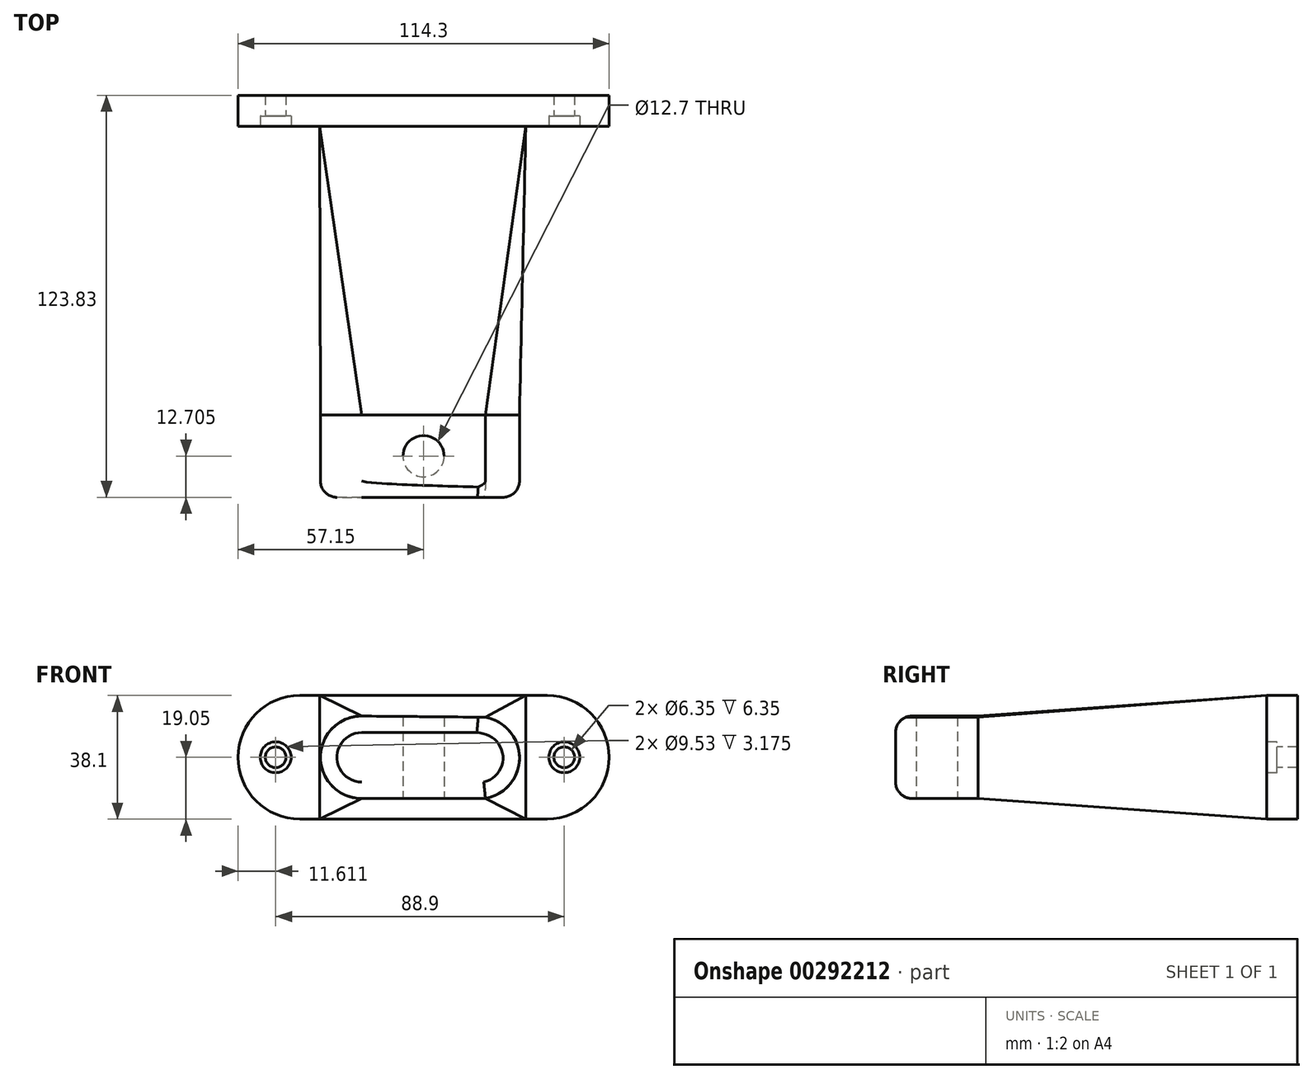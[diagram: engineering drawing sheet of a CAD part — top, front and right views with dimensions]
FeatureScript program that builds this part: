
annotation { "Feature Type Name" : "Feature", "Feature Type Description" : "" }
export const myFeature = defineFeature(function(context is Context, id is Id, definition is map)
    precondition{}
    {
        {
            var Q0;
            Q0=qCreatedBy(makeId("Front.planeOp"),FACE);
            var sketch = newSketch(context, id + "F0", { "sketchPlane" : qUnion([Q0])});
            skArc(sketch, "E0", {"start": v(0, 19.05) * mm, "mid": v(-19.05, 0) * mm, "end": v(0, -19.05) * mm});
            skLineSegment(sketch, "E1", {"start": v(0, 19.05) * mm, "end": v(76.2, 19.05) * mm});
            skArc(sketch, "E2", {"start": v(76.2, -19.05) * mm, "mid": v(95.25, 0) * mm, "end": v(76.2, 19.05) * mm});
            skLineSegment(sketch, "E3", {"start": v(0, -19.05) * mm, "end": v(76.2, -19.05) * mm});
            skSolve(sketch);
        }
        {
            var Q0;
            Q0 = qSketchRegion(id + "F0", true);
            extrude(context, id + "F1", {"entities" : qUnion([Q0]), "depth" : 9.52 * mm});
        }
        {
            var Q0;
            Q0=makeQuery(id+"F1.opExtrude","CAP_FACE",FACE,{"disambiguationData":[OSD([sQuery(id+"F0.wireOp",EDGE,"E0"),sQuery(id+"F0.wireOp",EDGE,"E1"),sQuery(id+"F0.wireOp",EDGE,"E2"),sQuery(id+"F0.wireOp",EDGE,"E3")])],"isStart":false});
            var sketch = newSketch(context, id + "F2", { "sketchPlane" : qUnion([Q0])});
            skPoint(sketch, "E4", {"position": v(-7.44, 0) * mm});
            skPoint(sketch, "E5", {"position": v(81.46, 0) * mm});
            skSolve(sketch);
        }
        {
            var Q0;
            Q0=sQuery(id+"F2.wireOp",VERTEX,"E4");
            var Q1;
            Q1=sQuery(id+"F2.wireOp",VERTEX,"E5");
            var Q2;
            Q2=makeQuery(id+"F1.opExtrude","SWEPT_BODY",BODY,{"disambiguationData":[OSD([sQuery(id+"F0.wireOp",EDGE,"E0"),sQuery(id+"F0.wireOp",EDGE,"E1"),sQuery(id+"F0.wireOp",EDGE,"E2"),sQuery(id+"F0.wireOp",EDGE,"E3")])]});
            hole(context, id + "F3", {"style" : HoleStyle.C_BORE, "endStyle" : HoleEndStyle.THROUGH, "holeDiameter" : 6.35 * mm, "cBoreDiameter" : 9.52 * mm, "cBoreDepth" : 3.17 * mm, "tappedDepth" : 12.7 * mm, "tapClearance" : 3, "locations" : qUnion([Q0, Q1]), "scope" : qUnion([Q2])});
        }
        {
            var Q0;
            Q0=makeQuery(id+"F1.opExtrude","CAP_FACE",FACE,{"disambiguationData":[OSD([sQuery(id+"F0.wireOp",EDGE,"E0"),sQuery(id+"F0.wireOp",EDGE,"E1"),sQuery(id+"F0.wireOp",EDGE,"E2"),sQuery(id+"F0.wireOp",EDGE,"E3")])],"isStart":false});
            var sketch = newSketch(context, id + "F4", { "sketchPlane" : qUnion([Q0])});
            skLineSegment(sketch, "E6", {"start": v(6.1, -19.05) * mm, "end": v(6.1, 19.05) * mm});
            skLineSegment(sketch, "E7", {"start": v(69.6, -19.05) * mm, "end": v(69.6, 19.05) * mm});
            skSolve(sketch);
        }
        {
            var Q0;
            {var subQ0=sQuery(id+"F4.wireOp",EDGE,"E6");Q0=makeQuery(id+"F4.imprint","IMPRINT",FACE,{"disambiguationData":[TD([[makeQuery(id+"F4.imprint","IMPRINT",EDGE,{"derivedFrom":subQ0}),-1.0]])]});}
            cPlane(context, id + "F5", {"entities" : qUnion([Q0]), "cplaneType" : CPlaneType.OFFSET, "offset" : 88.9 * mm, "width" : 152.4 * mm, "height" : 152.4 * mm});
        }
        {
            var Q0;
            Q0=qCreatedBy(id+"F5.planeOp",FACE);
            var sketch = newSketch(context, id + "F6", { "sketchPlane" : qUnion([Q0])});
            skArc(sketch, "E8", {"start": v(19.05, 12.7) * mm, "mid": v(6.35, 0) * mm, "end": v(19.05, -12.7) * mm});
            skLineSegment(sketch, "E9", {"start": v(19.05, 12.7) * mm, "end": v(57.15, 12.32) * mm});
            skLineSegment(sketch, "E10", {"start": v(19.05, -12.7) * mm, "end": v(57.15, -12.7) * mm});
            skArc(sketch, "E11", {"start": v(57.15, -12.7) * mm, "mid": v(67.66, -0.2) * mm, "end": v(57.15, 12.32) * mm});
            skSolve(sketch);
        }
        {
            var Q1;
            Q1=makeQuery(id+"F6.imprint","IMPRINT",FACE,{"disambiguationData":[TD([[makeQuery(id+"F6.imprint","IMPRINT",EDGE,{"derivedFrom":sQuery(id+"F6.wireOp",EDGE,"E8")}),1.0]])]});
            var Q2;
            {var subQ0=sQuery(id+"F4.wireOp",EDGE,"E6");Q2=makeQuery(id+"F4.imprint","IMPRINT",FACE,{"disambiguationData":[TD([[makeQuery(id+"F4.imprint","IMPRINT",EDGE,{"derivedFrom":subQ0}),-1.0]])]});}
            loft(context, id + "F7", {"operationType" : NewBodyOperationType.ADD, "sheetProfilesArray" : [{ "sheetProfileEntities" : qUnion([Q1]) }, { "sheetProfileEntities" : qUnion([Q2]) }]});
        }
        {
            var Q0;
            Q0=makeQuery(id+"F7.opLoft","CAP_FACE",FACE,{"disambiguationData":[OSD([makeQuery(id+"F6.imprint","IMPRINT",FACE,{"disambiguationData":[TD([[makeQuery(id+"F6.imprint","IMPRINT",EDGE,{"derivedFrom":sQuery(id+"F6.wireOp",EDGE,"E8")}),1.0]])]})])],"isStart":true});
            extrude(context, id + "F8", {"entities" : qUnion([Q0]), "operationType" : NewBodyOperationType.ADD, "depth" : 25.4 * mm});
        }
        {
            var Q0;
            Q0=makeQuery(id+"F8.opExtrude","SWEPT_FACE",FACE,{"disambiguationData":[OSD([sQuery(id+"F6.wireOp",EDGE,"E8"),sQuery(id+"F6.wireOp",EDGE,"E10"),sQuery(id+"F6.wireOp",EDGE,"E11")])]});
            var sketch = newSketch(context, id + "F9", { "sketchPlane" : qUnion([Q0])});
            skPoint(sketch, "E12", {"position": v(38.1, 123.83) * mm});
            skPoint(sketch, "E13", {"position": v(38.1, 111.13) * mm});
            skSolve(sketch);
        }
        {
            var Q0;
            Q0=sQuery(id+"F9.wireOp",VERTEX,"E13");
            var Q1;
            Q1=makeQuery(id+"F1.opExtrude","SWEPT_BODY",BODY,{"disambiguationData":[OSD([sQuery(id+"F0.wireOp",EDGE,"E0"),sQuery(id+"F0.wireOp",EDGE,"E1"),sQuery(id+"F0.wireOp",EDGE,"E2"),sQuery(id+"F0.wireOp",EDGE,"E3")])]});
            hole(context, id + "F10", {"style" : HoleStyle.SIMPLE, "endStyle" : HoleEndStyle.THROUGH, "holeDiameter" : 12.7 * mm, "tappedDepth" : 12.7 * mm, "tapClearance" : 3, "locations" : qUnion([Q0]), "scope" : qUnion([Q1])});
        }
        {
            var Q0;
            Q0=makeQuery(id+"F8.opExtrude","CAP_EDGE",EDGE,{"disambiguationData":[OSD([sQuery(id+"F6.wireOp",EDGE,"E8"),sQuery(id+"F6.wireOp",EDGE,"E10"),sQuery(id+"F6.wireOp",EDGE,"E11")])],"isStart":false});
            var Q1;
            Q1=makeQuery(id+"F8.opExtrude","CAP_EDGE",EDGE,{"disambiguationData":[OSD([sQuery(id+"F6.wireOp",EDGE,"E9"),sQuery(id+"F6.wireOp",EDGE,"E10"),sQuery(id+"F6.wireOp",EDGE,"E11")])],"isStart":false});
            fillet(context, id + "F11", {"entities" : qUnion([Q0, Q1]), "radius" : 5.08 * mm, "tangentPropagation" : true, "allowEdgeOverflow" : false});
        }
    });
